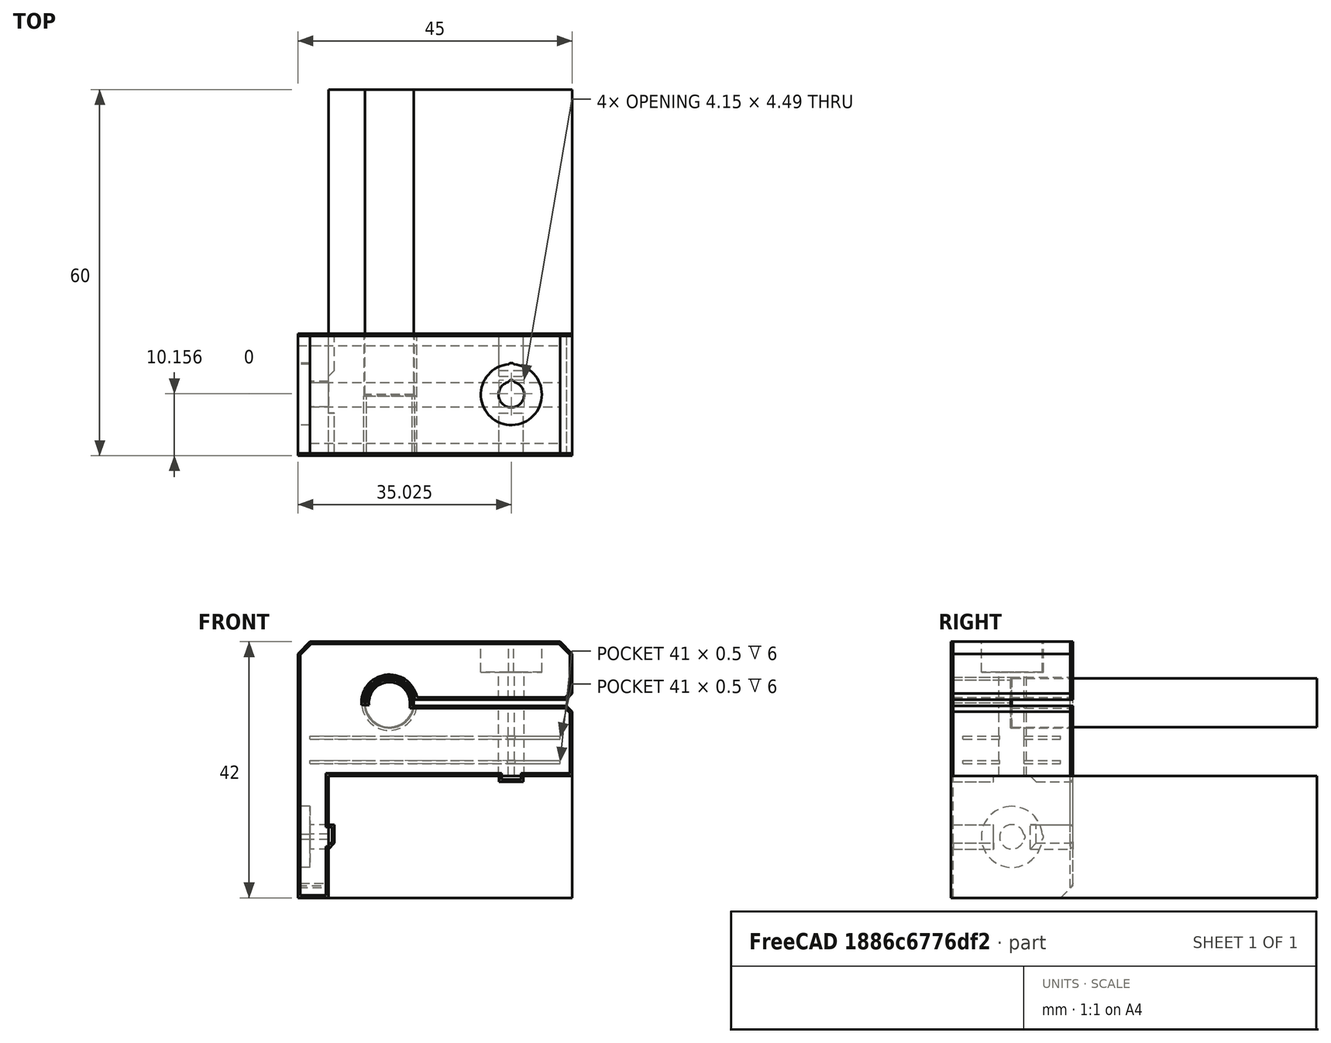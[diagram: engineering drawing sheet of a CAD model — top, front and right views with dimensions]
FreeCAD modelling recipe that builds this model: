
FCSTD DOCUMENT  (FreeCAD 0.18R14555 (Git shallow))
Label: rod-holder
License: All rights reserved
LicenseURL: http://en.wikipedia.org/wiki/All_rights_reserved
objects: Part::Box×13, Part::Cylinder×12, Part::Chamfer×9, Part::Cut×8, Part::MultiFuse×6, Part::Feature×1
note: 49 computed .brp shape members not serialized (recipe doc carries the construction recipe); baked Part::Feature solids carry a one-line shape summary decoded from their .brp

FEATURE [Part::Box] Box  label="profile"
  AttacherType = Attacher::AttachEngine3D
  Height = 20
  Length = 40
  Width = 60
FEATURE [Part::Cylinder] Cylinder  label="rod"
  Angle = 360
  AttacherType = Attacher::AttachEngine3D
  Height = 50
  Placement = pos=(10,10,32) rot=(-1,0,0;1.5708rad)
  Radius = 4
FEATURE [Part::Box] Box001  label="Cube"
  AttacherType = Attacher::AttachEngine3D
  Height = 22
  Length = 40
  Placement = pos=(0,0,20) rot=(0,0,1;0rad)
  Width = 20
FEATURE [Part::Box] Box002  label="Cube001"
  AttacherType = Attacher::AttachEngine3D
  Height = 42
  Length = 5
  Placement = pos=(-5,0,0) rot=(0,0,1;0rad)
  Width = 20
FEATURE [Part::MultiFuse] Fusion
  Shapes = -> [Box002,Box001]
FEATURE [Part::Cylinder] Cylinder001  label="slot"
  Angle = 360
  AttacherType = Attacher::AttachEngine3D
  Height = 10.2
  Placement = pos=(10,9.8,32) rot=(-1,0,0;1.5708rad)
  Radius = 4.15
FEATURE [Part::Cylinder] Cylinder002  label="Cylinder"
  Angle = 360
  AttacherType = Attacher::AttachEngine3D
  Height = 22
  Placement = pos=(30,10,20) rot=(0,0,1;0rad)
  Radius = 2.1
FEATURE [Part::Cylinder] Cylinder003  label="Cylinder001"
  Angle = 360
  AttacherType = Attacher::AttachEngine3D
  Height = 10
  Placement = pos=(30,10,37) rot=(0,0,1;0rad)
  Radius = 5
FEATURE [Part::Cylinder] Cylinder004  label="Cylinder002"
  Angle = 360
  AttacherType = Attacher::AttachEngine3D
  Height = 22
  Placement = pos=(30,11.9,20) rot=(0,0,1;0rad)
  Radius = 0.5
FEATURE [Part::Cylinder] Cylinder005  label="Cylinder003"
  Angle = 360
  AttacherType = Attacher::AttachEngine3D
  Height = 10
  Placement = pos=(30,14.7,37) rot=(0,0,1;0rad)
  Radius = 0.5
FEATURE [Part::Box] Box004  label="Cube003"
  AttacherType = Attacher::AttachEngine3D
  Height = 1
  Length = 34
  Placement = pos=(13.75,0,31.5) rot=(0,0,1;0rad)
  Width = 20
FEATURE [Part::Box] Box005  label="Cube004"
  AttacherType = Attacher::AttachEngine3D
  Height = 4
  Length = 1
  Placement = pos=(0,0,8) rot=(0,0,1;0rad)
  Width = 7
FEATURE [Part::Box] Box006  label="Cube005"
  AttacherType = Attacher::AttachEngine3D
  Height = 1
  Length = 4
  Placement = pos=(28,0,19) rot=(0,0,1;0rad)
  Width = 7
FEATURE [Part::Box] Box007  label="Cube006"
  AttacherType = Attacher::AttachEngine3D
  Height = 1
  Length = 4
  Placement = pos=(28,13,19) rot=(0,0,1;0rad)
  Width = 7
FEATURE [Part::Chamfer] Chamfer
  Base = -> Box007
  Edges = 1 edges r=0.99: [Edge9]
FEATURE [Part::Cylinder] Cylinder006  label="Cylinder004"
  Angle = 360
  AttacherType = Attacher::AttachEngine3D
  Height = 10
  Placement = pos=(3,11.7,10) rot=(0,-1,0;1.5708rad)
  Radius = 0.5
FEATURE [Part::Box] Box008  label="Cube007"
  AttacherType = Attacher::AttachEngine3D
  Height = 4
  Length = 1
  Placement = pos=(0,13,8) rot=(0,0,1;0rad)
  Width = 7
FEATURE [Part::Chamfer] Chamfer002
  Base = -> Box008
  Edges = 2 edges r=0.99: [Edge5,Edge8]
FEATURE [Part::Cylinder] Cylinder007  label="Cylinder005"
  Angle = 360
  AttacherType = Attacher::AttachEngine3D
  Height = 4
  Placement = pos=(-3,14.7,10) rot=(0,-1,0;1.5708rad)
  Radius = 0.5
FEATURE [Part::Cylinder] Cylinder008  label="Cylinder006"
  Angle = 360
  AttacherType = Attacher::AttachEngine3D
  Height = 4
  Placement = pos=(-3,10,10) rot=(0,-1,0;1.5708rad)
  Radius = 5
FEATURE [Part::Cylinder] Cylinder009  label="Cylinder007"
  Angle = 360
  AttacherType = Attacher::AttachEngine3D
  Height = 10
  Placement = pos=(3,10,10) rot=(0,-1,0;1.5708rad)
  Radius = 2
FEATURE [Part::MultiFuse] Fusion002
  Shapes = -> [Cylinder006,Cylinder007,Cylinder008,Cylinder009]
FEATURE [Part::MultiFuse] Fusion003
  Shapes = -> [Cylinder003,Cylinder002,Cylinder005,Cylinder004]
FEATURE [Part::Cylinder] Cylinder010  label="Cylinder008"
  Angle = 360
  AttacherType = Attacher::AttachEngine3D
  Height = 9.8
  Placement = pos=(10,7e-15,32) rot=(-1,0,0;1.5708rad)
  Radius = 4.2
FEATURE [Part::Cylinder] Cylinder011  label="Cylinder009"
  Angle = 360
  AttacherType = Attacher::AttachEngine3D
  Height = 9.8
  Placement = pos=(10,7e-15,32) rot=(-1,0,0;1.5708rad)
  Radius = 3.75
FEATURE [Part::Cut] Cut
  Base = -> Cylinder010
  Tool = -> Cylinder011
FEATURE [Part::Box] Box009  label="Cube008"
  AttacherType = Attacher::AttachEngine3D
  Height = 10
  Length = 10
  Placement = pos=(5,0,22) rot=(0,0,1;0rad)
  Width = 10
FEATURE [Part::Cut] Cut001
  Base = -> Cut
  Tool = -> Box009
FEATURE [Part::Cut] Cut002
  Base = -> Fusion
  Tool = -> Cylinder001
FEATURE [Part::Cut] Cut003
  Base = -> Cut002
  Tool = -> Cut001
FEATURE [Part::Cut] Cut004
  Base = -> Cut003
  Tool = -> Box004
FEATURE [Part::Cut] Cut005
  Base = -> Cut004
  Tool = -> Fusion003
FEATURE [Part::Cut] Cut006
  Base = -> Cut005
  Tool = -> Fusion002
FEATURE [Part::Chamfer] Chamfer003
  Base = -> Cut006
  Edges = 2 edges r=1: [Edge62,Edge79]
FEATURE [Part::Chamfer] Chamfer004
  Base = -> Chamfer003
  Edges = 1 edges r=2: [Edge39]
FEATURE [Part::Chamfer] Chamfer005
  Base = -> Chamfer004
  Edges = 1 edges r=2: [Edge63]
FEATURE [Part::Chamfer] Chamfer006
  Base = -> Chamfer005
  Edges = 1 edges r=2: [Edge36]
FEATURE [Part::Chamfer] Chamfer007
  Base = -> Box005
  Edges = 1 edges r=0.99: [Edge8]
FEATURE [Part::Box] Box010  label="Cube009"
  AttacherType = Attacher::AttachEngine3D
  Height = 0.5
  Length = 41
  Placement = pos=(-3,2,22) rot=(0,0,1;0rad)
  Width = 6
FEATURE [Part::Box] Box012  label="Cube011"
  AttacherType = Attacher::AttachEngine3D
  Height = 0.5
  Length = 41
  Placement = pos=(-3,2,26) rot=(0,0,1;0rad)
  Width = 6
FEATURE [Part::Box] Box013  label="Cube012"
  AttacherType = Attacher::AttachEngine3D
  Height = 0.5
  Length = 41
  Placement = pos=(-3,12,22) rot=(0,0,1;0rad)
  Width = 6
FEATURE [Part::Box] Box015  label="Cube014"
  AttacherType = Attacher::AttachEngine3D
  Height = 0.5
  Length = 41
  Placement = pos=(-3,12,26) rot=(0,0,1;0rad)
  Width = 6
FEATURE [Part::MultiFuse] Fusion004
  Shapes = -> [Chamfer007,Chamfer002,Box006,Chamfer]
FEATURE [Part::MultiFuse] Fusion005
  Shapes = -> [Chamfer006,Fusion004]
FEATURE [Part::MultiFuse] Fusion006
  Shapes = -> [Box010,Box012,Box015,Box013]
FEATURE [Part::Cut] Cut007
  Base = -> Fusion005
  Tool = -> Fusion006
FEATURE [Part::Feature] Cut007001  label="Cut008"
  shape: bbox 45 x 20 x 42 mm, 85 faces (baked)
FEATURE [Part::Chamfer] Chamfer008
  Base = -> Cut007001
  Edges = 2 edges r=0.4: [Edge77,Edge98]
FEATURE [Part::Chamfer] Chamfer009
  Base = -> Chamfer008
  Edges = 52 edges r=0.4: [Edge1,Edge5,Edge11,Edge12,Edge13,Edge14,Edge15,Edge16,Edge17,Edge18,Edge19,Edge20,Edge21,Edge22,Edge23,Edge24,Edge25,Edge26,Edge27,Edge28,Edge29,Edge30,Edge31,Edge32,Edge33,Edge34,Edge38,Edge43,Edge44,Edge45,Edge46,Edge47,Edge48,Edge49,Edge50,Edge51,Edge52,Edge53,Edge54,Edge55,Edge56,Edge57,Edge58,+9 more]
